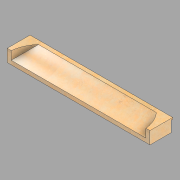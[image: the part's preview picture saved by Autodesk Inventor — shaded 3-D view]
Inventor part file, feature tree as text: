
AUTODESK INVENTOR PART (.ipt)
format: ipt  version: 2022.2 (Build 262287010, 287A)  size: 136,704 bytes
history: native  units: in
note: dims shown in document units (in); Inventor stores cm internally (conversion verified against a paired STEP export)
features: revolve x2, other x1, direct_edit x1
ambient origin geometry x8: Origin, YZ Plane, XZ Plane, XY Plane, X Axis, Y Axis, Z Axis, Center Point
bodies: Solid1 (feature_tree)
feature tree (4):
  other  "West (2)"
  direct_edit  "Direct Edit1"
  revolve  "Rotate1"  [1 undecoded]
  revolve  "Rotate2"  Angle=90.0deg
note: 1 required parameter value undecoded (feature->parameter linkage not recoverable at this tier; creation-order binding heuristic only, values carry confidence <= 0.55)
